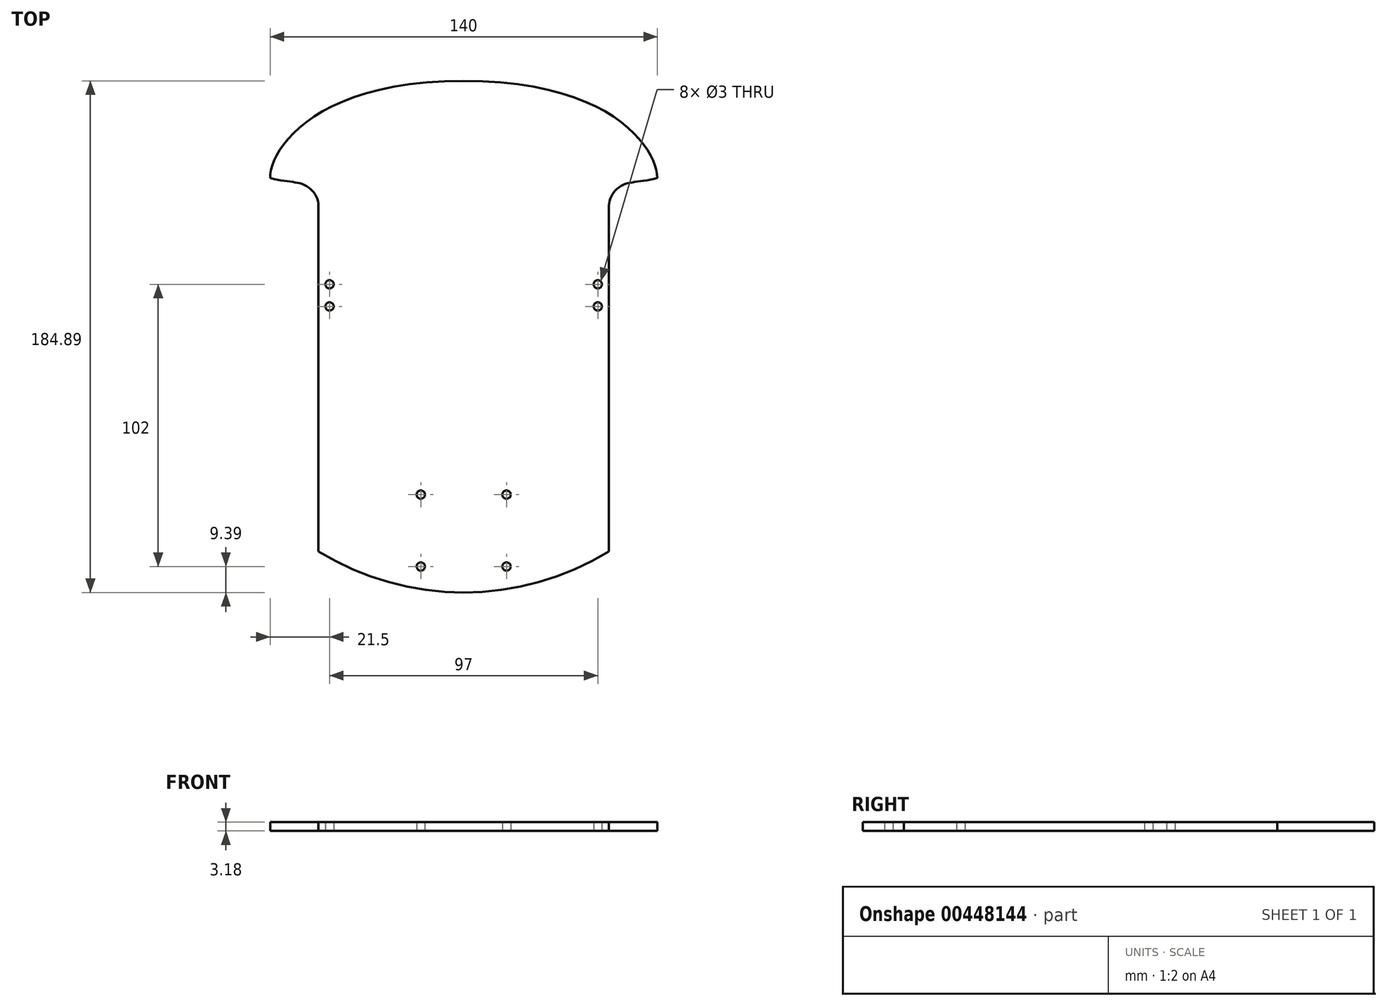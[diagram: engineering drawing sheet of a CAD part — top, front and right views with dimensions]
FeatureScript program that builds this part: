
annotation { "Feature Type Name" : "Feature", "Feature Type Description" : "" }
export const myFeature = defineFeature(function(context is Context, id is Id, definition is map)
    precondition{}
    {
        {
            var Q0;
            Q0=qCreatedBy(makeId("Top.planeOp"),FACE);
            var sketch = newSketch(context, id + "F0", { "sketchPlane" : qUnion([Q0])});
            skLineSegment(sketch, "E0.bottom", {"start": v(52.5, 62.5) * mm, "end": v(-52.5, 62.5) * mm, "construction": true});
            skLineSegment(sketch, "E0.top", {"start": v(52.5, -62.5) * mm, "end": v(-52.5, -62.5) * mm, "construction": true});
            skLineSegment(sketch, "E0.left", {"start": v(52.5, 62.5) * mm, "end": v(52.5, -62.5) * mm});
            skLineSegment(sketch, "E0.right", {"start": v(-52.5, 62.5) * mm, "end": v(-52.5, -62.5) * mm});
            skPoint(sketch, "E0.middle", {"position": v(0, 0) * mm});
            skArc(sketch, "E1", {"start": v(-52.5, -62.5) * mm, "mid": v(0, -77.39) * mm, "end": v(52.5, -62.5) * mm});
            skFitSpline(sketch, "E2", {"points": [v(-70, 72.5) * mm, v(0, 107.5) * mm], "startDerivative": vector(0, 29.15) * mm, "endDerivative": vector(164.4, 0) * mm});
            skFitSpline(sketch, "E3", {"points": [v(-70, 72.5) * mm, v(-56.93, 69.6) * mm, v(-52.5, 62.5) * mm], "startDerivative": vector(31.94, -9.6) * mm, "endDerivative": vector(0, -18.1) * mm});
            skFitSpline(sketch, "E4.MirrorCS", {"points": [v(70, 72.5) * mm, v(56.93, 69.6) * mm, v(52.5, 62.5) * mm], "startDerivative": vector(-31.94, -9.6) * mm, "endDerivative": vector(0, -18.1) * mm});
            skFitSpline(sketch, "E5.MirrorCS", {"points": [v(70, 72.5) * mm, v(0, 107.5) * mm], "startDerivative": vector(0, 29.15) * mm, "endDerivative": vector(-164.4, 0) * mm});
            skSolve(sketch);
        }
        {
            var Q0;
            Q0=makeQuery(id+"F0.imprint","IMPRINT",FACE,{"disambiguationData":[TD([[makeQuery(id+"F0.imprint","IMPRINT",EDGE,{"derivedFrom":sQuery(id+"F0.wireOp",EDGE,"E0.left")}),-1.0]])]});
            var Q1;
            Q1 = qConstructionFilter(qBodyType(qCreatedBy(id + "F0" ,EDGE), BodyType.WIRE), ConstructionObject.NO);
            extrude(context, id + "F1", {"entities" : qUnion([Q0]), "surfaceEntities" : qUnion([Q1]), "depth" : 3.17 * mm});
        }
        {
            var Q0;
            Q0=qCreatedBy(makeId("Top.planeOp"),FACE);
            var sketch = newSketch(context, id + "F2", { "sketchPlane" : qUnion([Q0])});
            skCircle(sketch, "E6", {"center": v(-15.5, -42) * mm, "radius": 1.5 * mm});
            skLineSegment(sketch, "E7", {"start": v(-10.28, -55) * mm, "end": v(7.03, -55) * mm, "construction": true});
            skCircle(sketch, "E8.MirrorC", {"center": v(15.5, -42) * mm, "radius": 1.5 * mm});
            skCircle(sketch, "E9.MirrorC", {"center": v(-15.5, -68) * mm, "radius": 1.5 * mm});
            skCircle(sketch, "E10.MirrorC", {"center": v(15.5, -68) * mm, "radius": 1.5 * mm});
            skSolve(sketch);
        }
        {
            var Q0;
            Q0=qCreatedBy(makeId("Top.planeOp"),FACE);
            var sketch = newSketch(context, id + "F3", { "sketchPlane" : qUnion([Q0])});
            skCircle(sketch, "E11", {"center": v(-48.5, 34) * mm, "radius": 1.5 * mm});
            skLineSegment(sketch, "E12", {"start": v(-52.5, 30) * mm, "end": v(-33.64, 30) * mm, "construction": true});
            skCircle(sketch, "E13.MirrorC", {"center": v(-48.5, 26) * mm, "radius": 1.5 * mm});
            skCircle(sketch, "E14.MirrorC", {"center": v(48.5, 26) * mm, "radius": 1.5 * mm});
            skCircle(sketch, "E15.MirrorC", {"center": v(48.5, 34) * mm, "radius": 1.5 * mm});
            skSolve(sketch);
        }
        {
            var Q0;
            Q0 = qSketchRegion(id + "F2", true);
            var Q1;
            Q1 = qSketchRegion(id + "F3", true);
            extrude(context, id + "F4", {"entities" : qUnion([Q0, Q1]), "operationType" : NewBodyOperationType.REMOVE, "endBound" : BoundingType.THROUGH_ALL, "depth" : 25 * mm});
        }
    });
